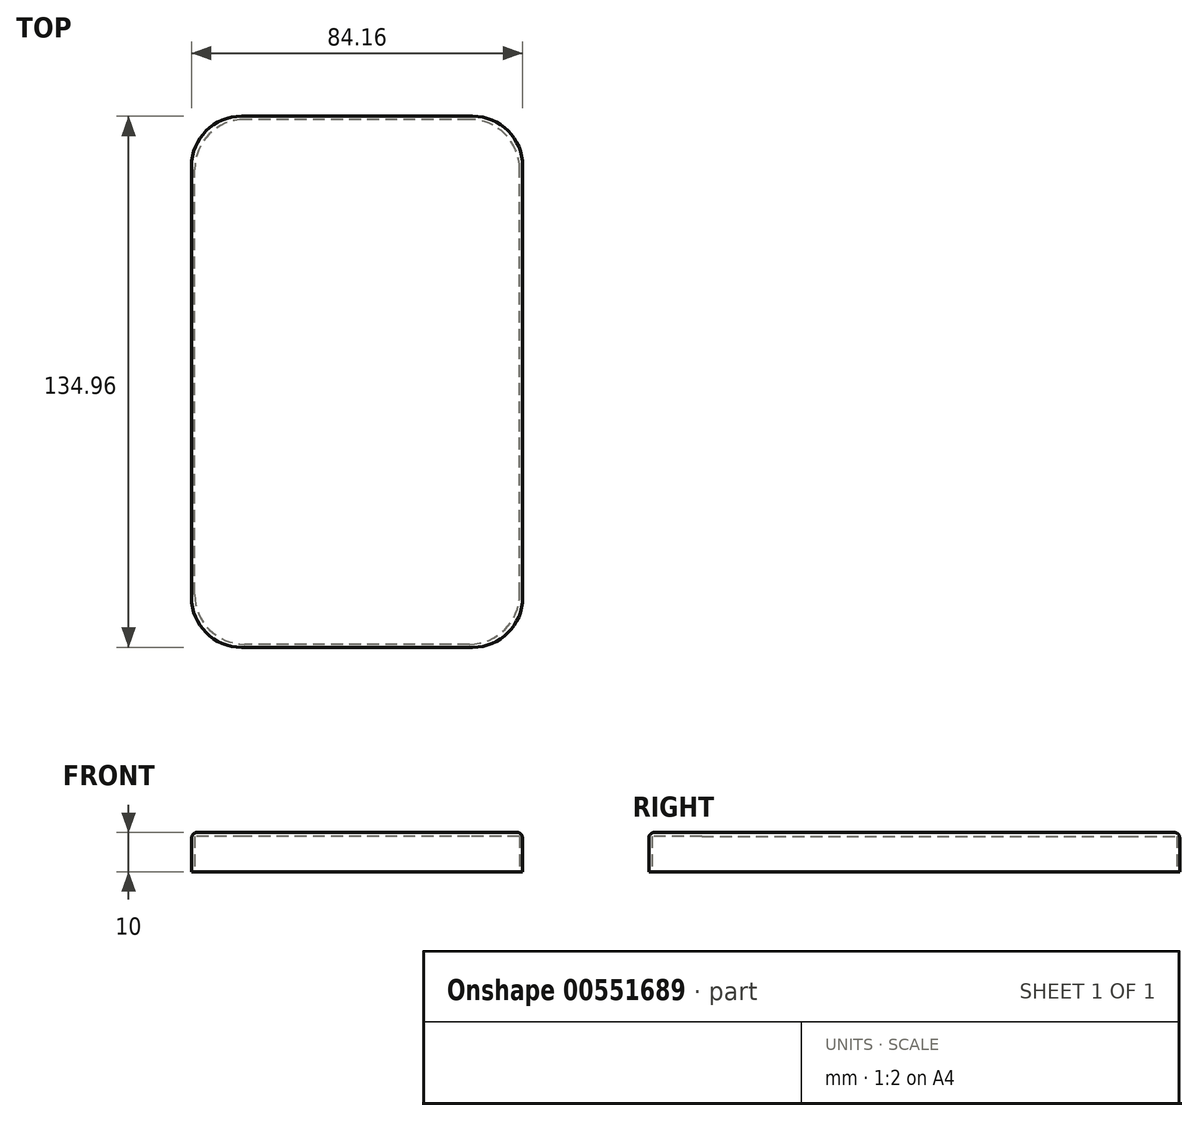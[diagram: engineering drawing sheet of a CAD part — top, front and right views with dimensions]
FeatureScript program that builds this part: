
annotation { "Feature Type Name" : "Feature", "Feature Type Description" : "" }
export const myFeature = defineFeature(function(context is Context, id is Id, definition is map)
    precondition{}
    {
        {
            var Q0;
            Q0=qCreatedBy(makeId("Top.planeOp"),FACE);
            var sketch = newSketch(context, id + "F0", { "sketchPlane" : qUnion([Q0])});
            skLineSegment(sketch, "E0.bottom", {"start": v(29.38, 67.48) * mm, "end": v(-29.38, 67.48) * mm});
            skLineSegment(sketch, "E0.top", {"start": v(29.38, -67.48) * mm, "end": v(-29.38, -67.48) * mm});
            skLineSegment(sketch, "E0.left", {"start": v(42.08, 54.78) * mm, "end": v(42.08, -54.78) * mm});
            skLineSegment(sketch, "E0.right", {"start": v(-42.08, 54.78) * mm, "end": v(-42.08, -54.78) * mm});
            skPoint(sketch, "E0.middle", {"position": v(0, 0) * mm});
            skPoint(sketch, "E1.visualSharp", {"position": v(-42.08, 67.48) * mm});
            skArc(sketch, "E1.filletArc", {"start": v(-29.38, 67.48) * mm, "mid": v(-38.36, 63.76) * mm, "end": v(-42.08, 54.78) * mm});
            skPoint(sketch, "E2.visualSharp", {"position": v(42.08, 67.48) * mm});
            skArc(sketch, "E2.filletArc", {"start": v(42.08, 54.78) * mm, "mid": v(38.36, 63.76) * mm, "end": v(29.38, 67.48) * mm});
            skPoint(sketch, "E3.visualSharp", {"position": v(42.08, -67.48) * mm});
            skArc(sketch, "E3.filletArc", {"start": v(29.38, -67.48) * mm, "mid": v(38.36, -63.76) * mm, "end": v(42.08, -54.78) * mm});
            skPoint(sketch, "E4.visualSharp", {"position": v(-42.08, -67.48) * mm});
            skArc(sketch, "E4.filletArc", {"start": v(-42.08, -54.78) * mm, "mid": v(-38.36, -63.76) * mm, "end": v(-29.38, -67.48) * mm});
            skSolve(sketch);
        }
        {
            var Q0;
            Q0=makeQuery(id+"F0.imprint","IMPRINT",FACE,{"disambiguationData":[TD([[makeQuery(id+"F0.imprint","IMPRINT",EDGE,{"derivedFrom":sQuery(id+"F0.wireOp",EDGE,"E0.bottom")}),1.0]])]});
            extrude(context, id + "F1", {"entities" : qUnion([Q0]), "depth" : 10 * mm});
        }
        {
            var Q0;
            Q0=makeQuery(id+"F1.opExtrude","CAP_EDGE",EDGE,{"disambiguationData":[OSD([sQuery(id+"F0.wireOp",EDGE,"E0.left")])],"isStart":false});
            var Q1;
            Q1=makeQuery(id+"F1.opExtrude","CAP_EDGE",EDGE,{"disambiguationData":[OSD([sQuery(id+"F0.wireOp",EDGE,"E3.filletArc")])],"isStart":false});
            var Q2;
            Q2=makeQuery(id+"F1.opExtrude","CAP_EDGE",EDGE,{"disambiguationData":[OSD([sQuery(id+"F0.wireOp",EDGE,"E0.top")])],"isStart":false});
            var Q3;
            Q3=makeQuery(id+"F1.opExtrude","CAP_EDGE",EDGE,{"disambiguationData":[OSD([sQuery(id+"F0.wireOp",EDGE,"E4.filletArc")])],"isStart":false});
            var Q4;
            Q4=makeQuery(id+"F1.opExtrude","CAP_EDGE",EDGE,{"disambiguationData":[OSD([sQuery(id+"F0.wireOp",EDGE,"E0.right")])],"isStart":false});
            var Q5;
            Q5=makeQuery(id+"F1.opExtrude","CAP_EDGE",EDGE,{"disambiguationData":[OSD([sQuery(id+"F0.wireOp",EDGE,"E1.filletArc")])],"isStart":false});
            var Q6;
            Q6=makeQuery(id+"F1.opExtrude","CAP_EDGE",EDGE,{"disambiguationData":[OSD([sQuery(id+"F0.wireOp",EDGE,"E0.bottom")])],"isStart":false});
            var Q7;
            Q7=makeQuery(id+"F1.opExtrude","CAP_EDGE",EDGE,{"disambiguationData":[OSD([sQuery(id+"F0.wireOp",EDGE,"E2.filletArc")])],"isStart":false});
            fillet(context, id + "F2", {"entities" : qUnion([Q0, Q1, Q2, Q3, Q4, Q5, Q6, Q7]), "radius" : 1.59 * mm, "tangentPropagation" : true, "allowEdgeOverflow" : false});
        }
        {
            var Q0;
            Q0=qCreatedBy(makeId("Top.planeOp"),FACE);
            var sketch = newSketch(context, id + "F3", { "sketchPlane" : qUnion([Q0])});
            skLineSegment(sketch, "E5.bottom", {"start": v(28.58, -66.68) * mm, "end": v(-28.58, -66.68) * mm});
            skLineSegment(sketch, "E5.top", {"start": v(28.58, 66.68) * mm, "end": v(-28.57, 66.68) * mm});
            skLineSegment(sketch, "E5.left", {"start": v(41.28, -53.98) * mm, "end": v(41.28, 53.98) * mm});
            skLineSegment(sketch, "E5.right", {"start": v(-41.27, -53.98) * mm, "end": v(-41.27, 53.98) * mm});
            skPoint(sketch, "E5.middle", {"position": v(0, 0) * mm});
            skPoint(sketch, "E6.visualSharp", {"position": v(-41.27, 66.68) * mm});
            skArc(sketch, "E6.filletArc", {"start": v(-28.57, 66.67) * mm, "mid": v(-37.56, 62.96) * mm, "end": v(-41.27, 53.98) * mm});
            skPoint(sketch, "E7.visualSharp", {"position": v(41.28, 66.68) * mm});
            skArc(sketch, "E7.filletArc", {"start": v(41.28, 53.98) * mm, "mid": v(37.56, 62.96) * mm, "end": v(28.58, 66.68) * mm});
            skPoint(sketch, "E8.visualSharp", {"position": v(41.28, -66.68) * mm});
            skArc(sketch, "E8.filletArc", {"start": v(28.58, -66.67) * mm, "mid": v(37.56, -62.96) * mm, "end": v(41.28, -53.98) * mm});
            skPoint(sketch, "E9.visualSharp", {"position": v(-41.28, -66.68) * mm});
            skArc(sketch, "E9.filletArc", {"start": v(-41.28, -53.98) * mm, "mid": v(-37.56, -62.96) * mm, "end": v(-28.58, -66.68) * mm});
            skSolve(sketch);
        }
        {
            var Q0;
            Q0=makeQuery(id+"F3.imprint","IMPRINT",FACE,{"disambiguationData":[TD([[makeQuery(id+"F3.imprint","IMPRINT",EDGE,{"derivedFrom":sQuery(id+"F3.wireOp",EDGE,"E5.bottom")}),-1.0]])]});
            extrude(context, id + "F4", {"entities" : qUnion([Q0]), "operationType" : NewBodyOperationType.REMOVE, "depth" : 9 * mm});
        }
    });
